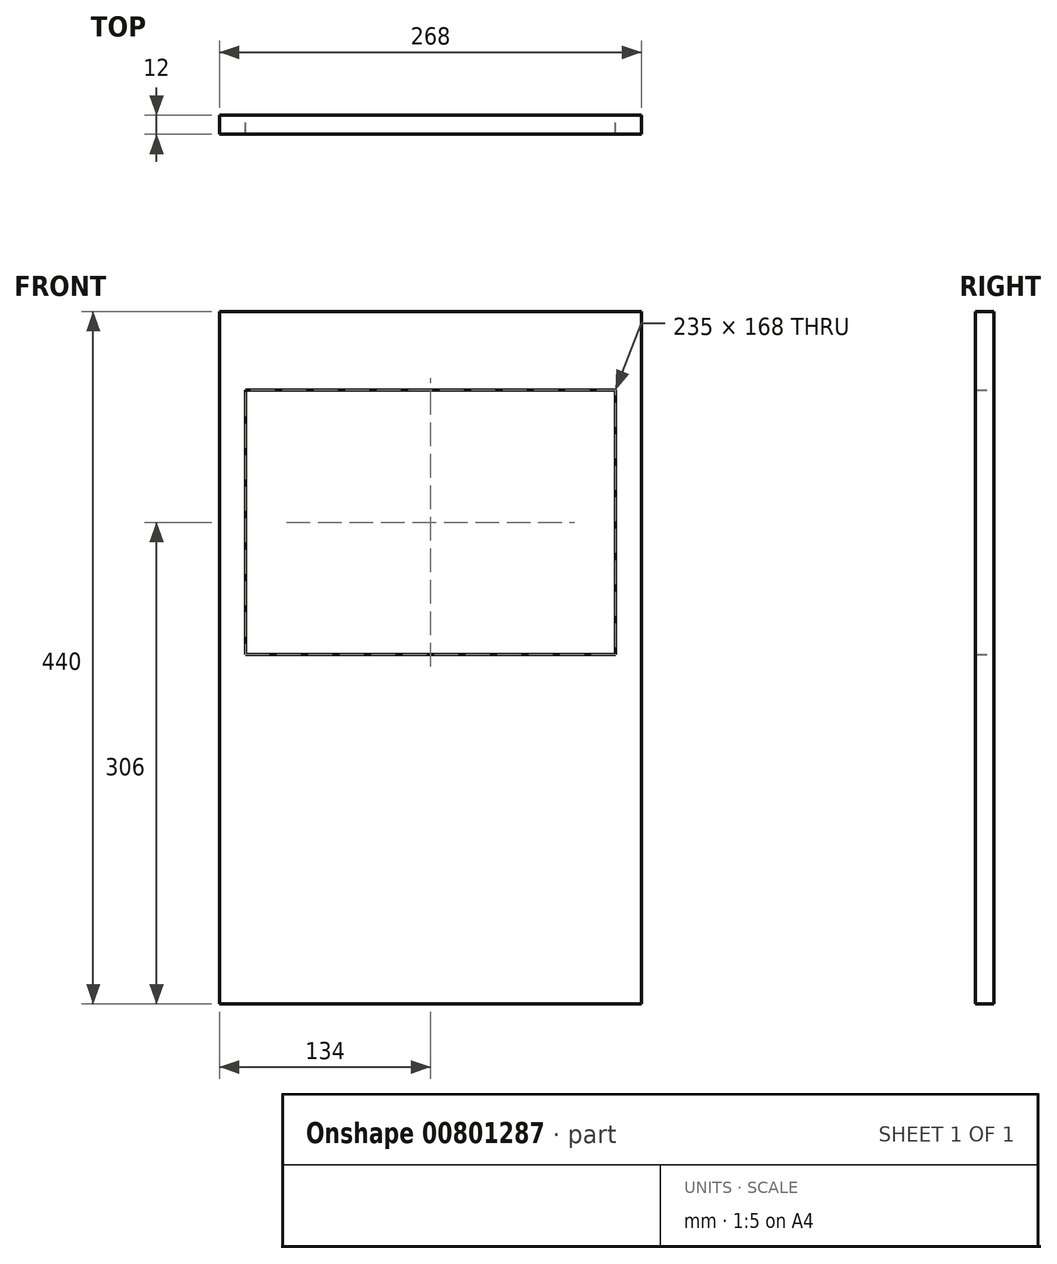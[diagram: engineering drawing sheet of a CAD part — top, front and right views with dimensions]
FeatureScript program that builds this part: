
annotation { "Feature Type Name" : "Feature", "Feature Type Description" : "" }
export const myFeature = defineFeature(function(context is Context, id is Id, definition is map)
    precondition{}
    {
        {
            var Q0;
            Q0=qCreatedBy(makeId("Front.planeOp"),FACE);
            var sketch = newSketch(context, id + "F0", { "sketchPlane" : qUnion([Q0])});
            skLineSegment(sketch, "E0.bottom", {"start": v(-134, -220) * mm, "end": v(134, -220) * mm});
            skLineSegment(sketch, "E0.top", {"start": v(-134, 220) * mm, "end": v(134, 220) * mm});
            skLineSegment(sketch, "E0.left", {"start": v(-134, -220) * mm, "end": v(-134, 220) * mm});
            skLineSegment(sketch, "E0.right", {"start": v(134, -220) * mm, "end": v(134, 220) * mm});
            skPoint(sketch, "E0.middle", {"position": v(0, 0) * mm});
            skLineSegment(sketch, "E1.bottom", {"start": v(-127.5, -8) * mm, "end": v(127.5, -8) * mm});
            skLineSegment(sketch, "E1.top", {"start": v(-127.5, 180) * mm, "end": v(127.5, 180) * mm});
            skLineSegment(sketch, "E1.left", {"start": v(-127.5, -8) * mm, "end": v(-127.5, 180) * mm});
            skLineSegment(sketch, "E1.right", {"start": v(127.5, -8) * mm, "end": v(127.5, 180) * mm});
            skPoint(sketch, "E1.middle", {"position": v(0, 86) * mm});
            skLineSegment(sketch, "E2.bottom", {"start": v(-117.5, 2) * mm, "end": v(117.5, 2) * mm});
            skLineSegment(sketch, "E2.top", {"start": v(-117.5, 170) * mm, "end": v(117.5, 170) * mm});
            skLineSegment(sketch, "E2.left", {"start": v(-117.5, 2) * mm, "end": v(-117.5, 170) * mm});
            skLineSegment(sketch, "E2.right", {"start": v(117.5, 2) * mm, "end": v(117.5, 170) * mm});
            skSolve(sketch);
        }
        {
            var Q0;
            Q0=makeQuery(id+"F0.imprint","IMPRINT",FACE,{"disambiguationData":[TD([[makeQuery(id+"F0.imprint","IMPRINT",EDGE,{"derivedFrom":sQuery(id+"F0.wireOp",EDGE,"E0.bottom")}),1.0]])]});
            var Q1;
            Q1=makeQuery(id+"F0.imprint","IMPRINT",FACE,{"disambiguationData":[TD([[makeQuery(id+"F0.imprint","IMPRINT",EDGE,{"derivedFrom":sQuery(id+"F0.wireOp",EDGE,"E1.bottom")}),1.0]])]});
            extrude(context, id + "F1", {"entities" : qUnion([Q0, Q1]), "depth" : 12 * mm, "offsetDistance" : 25 * mm});
        }
    });
